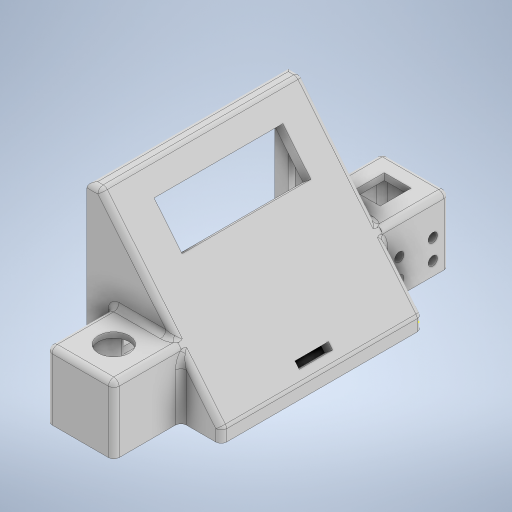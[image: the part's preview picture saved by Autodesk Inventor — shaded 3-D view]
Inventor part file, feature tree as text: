
AUTODESK INVENTOR PART (.ipt)
format: ipt  version: 2024.1 (Build 281209000, 209)  size: 635,904 bytes
history: native  units: mm
features: sketch x17, extrude x16, other x1, fillet x1
ambient origin geometry x8: Origin, YZ Plane, XZ Plane, XY Plane, X Axis, Y Axis, Z Axis, Center Point
bodies: Body1 (feature_tree)
feature tree (35):
  other  "Sólido1"
  extrude  "Extrusão1"  Depth=150.0mm
  extrude  "Extrusão2"  Depth=10.0mm
  extrude  "Extrusão27"  Depth=5.0mm
  extrude  "Extrusão28"  Depth=10.0mm TaperAngle=0.0deg
  extrude  "Extrusão29"  Depth=76.0mm
  sketch  "Esboço37"  dims[d175=10.0mm d176=33.0mm]
  extrude  "Extrusão30"  Depth=10.0mm
  extrude  "Extrusão31"  Depth=96.0mm
  extrude  "Extrusão32"  Depth=2.0mm
  extrude  "Extrusão33"  Depth=25.0mm
  extrude  "Extrusão34"  Depth=25.0mm
  extrude  "Extrusão35"  Depth=10.0mm
  extrude  "Extrusão36"  Depth=10.0mm
  extrude  "Extrusão37"  Depth=10.0mm TaperAngle=0.0deg
  extrude  "Extrusão38"  Depth=80.0mm
  extrude  "Extrusão39"  Depth=10.0mm TaperAngle=0.0deg
  extrude  "Extrusão40"  Depth=10.0mm
  fillet  "Arredondamento8"  Radius=10.0mm
  sketch  "Esboço1"  dims[d0=100.0mm d1=150.0mm]
  sketch  "Esboço2"  dims[d2=10.0mm d3=0.0mm d4=110.0mm]
  sketch  "Esboço34"  dims[d5=15.0mm d6=5.0mm]
  sketch  "Esboço35"  dims[d7=10.0mm d8=150.0mm d9=0.0mm]
  sketch  "Esboço36"  dims[d173=5.0mm d174=76.0mm]
  sketch  "Esboço38"  dims[d177=46.5mm d178=96.0mm]
  sketch  "Esboço39"  dims[d179=33.0mm d180=2.0mm]
  sketch  "Esboço40"  dims[d181=12.5mm d182=25.0mm]
  sketch  "Esboço41"  dims[d183=5.0mm d184=25.0mm]
  sketch  "Esboço42"  dims[d185=10.0mm d186=0.0mm d187=10.0mm]
  sketch  "Esboço43"  dims[d188=10.0mm d189=10.0mm]
  sketch  "Esboço44"  dims[d190=10.0mm d191=10.0mm d192=0.0mm]
  sketch  "Esboço45"  dims[d193=5.0mm d194=80.0mm]
  sketch  "Esboço46"  dims[d195=10.0mm d196=0.0mm d197=5.0mm d198=0.0mm]
  sketch  "Esboço47"  dims[d199=5.0mm d200=0.0mm d201=20.0mm d202=10.0mm]
  sketch  "Esboço48"  dims[d203=40.0mm d204=10.0mm d205=50.0mm d206=40.0mm d207=10.0mm d208=50.0mm d209=0.0mm d210=30.0mm d211=50.0mm d212=50.0mm d213=50.0mm d214=50.0mm d215=0.0mm d216=23.0mm d217=50.0mm d218=0.0mm d219=5.0mm d220=5.0mm d221=5.0mm d222=5.0mm d223=46.0mm d224=0.0mm d225=5.0mm d226=5.0mm d227=5.0mm d228=5.0mm d229=45.0mm d230=0.0mm d231=10.0mm d232=0.0mm d233=10.0mm d234=0.0mm d235=10.0mm d236=20.0mm d237=11.5mm d238=23.0mm d239=10.0mm d240=0.0mm d241=25.0mm d242=25.0mm d243=15.0mm d244=12.5mm d245=25.0mm d246=7.0mm d247=7.0mm d248=7.0mm d249=7.0mm d250=5.0mm d251=0.0mm d252=4.0mm d10=0.5mm d11=0.872665mm]
